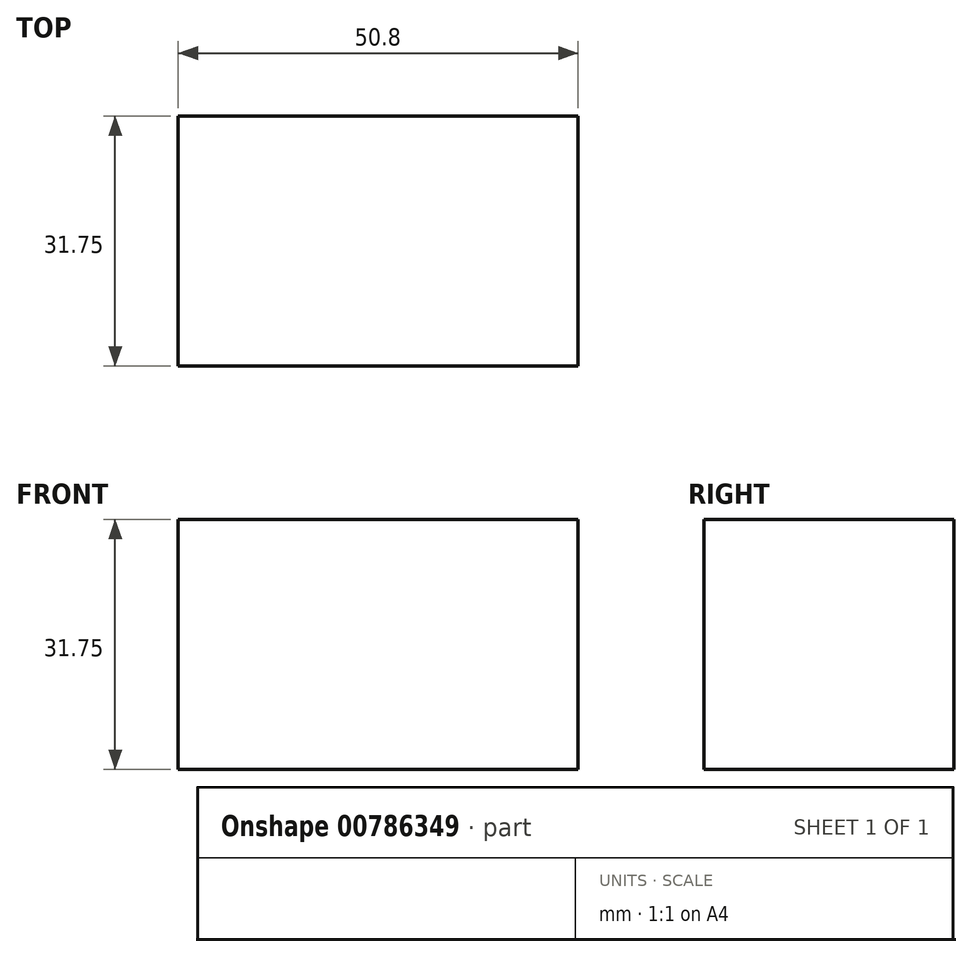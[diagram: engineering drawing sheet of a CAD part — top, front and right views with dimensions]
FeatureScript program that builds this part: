
annotation { "Feature Type Name" : "Feature", "Feature Type Description" : "" }
export const myFeature = defineFeature(function(context is Context, id is Id, definition is map)
    precondition{}
    {
        {
            var Q0;
            Q0=qCreatedBy(makeId("Front.planeOp"),FACE);
            var sketch = newSketch(context, id + "F0", { "sketchPlane" : qUnion([Q0])});
            skLineSegment(sketch, "E0", {"start": v(0, 0) * mm, "end": v(0, 31.75) * mm});
            skLineSegment(sketch, "E1", {"start": v(0, 31.75) * mm, "end": v(50.8, 31.75) * mm});
            skLineSegment(sketch, "E2", {"start": v(50.8, 31.75) * mm, "end": v(50.8, 0) * mm});
            skLineSegment(sketch, "E3", {"start": v(50.8, 0) * mm, "end": v(0, 0) * mm});
            skSolve(sketch);
        }
        {
            var Q0;
            Q0=makeQuery(id+"F0.imprint","IMPRINT",FACE,{"disambiguationData":[TD([[makeQuery(id+"F0.imprint","IMPRINT",EDGE,{"derivedFrom":sQuery(id+"F0.wireOp",EDGE,"E0")}),-1.0]])]});
            extrude(context, id + "F1", {"entities" : qUnion([Q0]), "depth" : 31.75 * mm, "offsetDistance" : 25.4 * mm});
        }
        {
            var Q0;
            Q0=makeQuery(id+"F1.opExtrude","CAP_FACE",FACE,{"disambiguationData":[OSD([sQuery(id+"F0.wireOp",EDGE,"E0"),sQuery(id+"F0.wireOp",EDGE,"E1"),sQuery(id+"F0.wireOp",EDGE,"E2"),sQuery(id+"F0.wireOp",EDGE,"E3")])],"isStart":true});
            var sketch = newSketch(context, id + "F2", { "sketchPlane" : qUnion([Q0])});
            skLineSegment(sketch, "E4", {"start": v(0, 31.75) * mm, "end": v(-12.7, 31.75) * mm});
            skLineSegment(sketch, "E5", {"start": v(0, 0) * mm, "end": v(0, 12.7) * mm});
            skLineSegment(sketch, "E6", {"start": v(0, 12.7) * mm, "end": v(-12.7, 31.75) * mm});
            skSolve(sketch);
        }
        {
            var Q0;
            {var subQ0=sQuery(id+"F2.wireOp",EDGE,"E4");Q0=makeQuery(id+"F2.imprint","IMPRINT",FACE,{"disambiguationData":[TD([[makeQuery(id+"F2.imprint","IMPRINT",EDGE,{"derivedFrom":subQ0}),1.0]])]});}
            extrude(context, id + "F3", {"entities" : qUnion([Q0]), "operationType" : NewBodyOperationType.REMOVE, "oppositeDirection" : true, "depth" : 12.7 * mm, "offsetDistance" : 25.4 * mm});
        }
        {
            var Q0;
            Q0=makeQuery(id+"F3.boolean.opBoolean","COPY",FACE,{"derivedFrom":makeQuery(id+"F3.opExtrude","CAP_FACE",FACE,{"disambiguationData":[OSD([sQuery(id+"F0.wireOp",EDGE,"E0"),sQuery(id+"F2.wireOp",EDGE,"E4"),sQuery(id+"F2.wireOp",EDGE,"E6")])],"isStart":false})});
            extrude(context, id + "F4", {"entities" : qUnion([Q0]), "operationType" : NewBodyOperationType.ADD, "depth" : 12.7 * mm, "offsetDistance" : 25.4 * mm});
        }
    });
